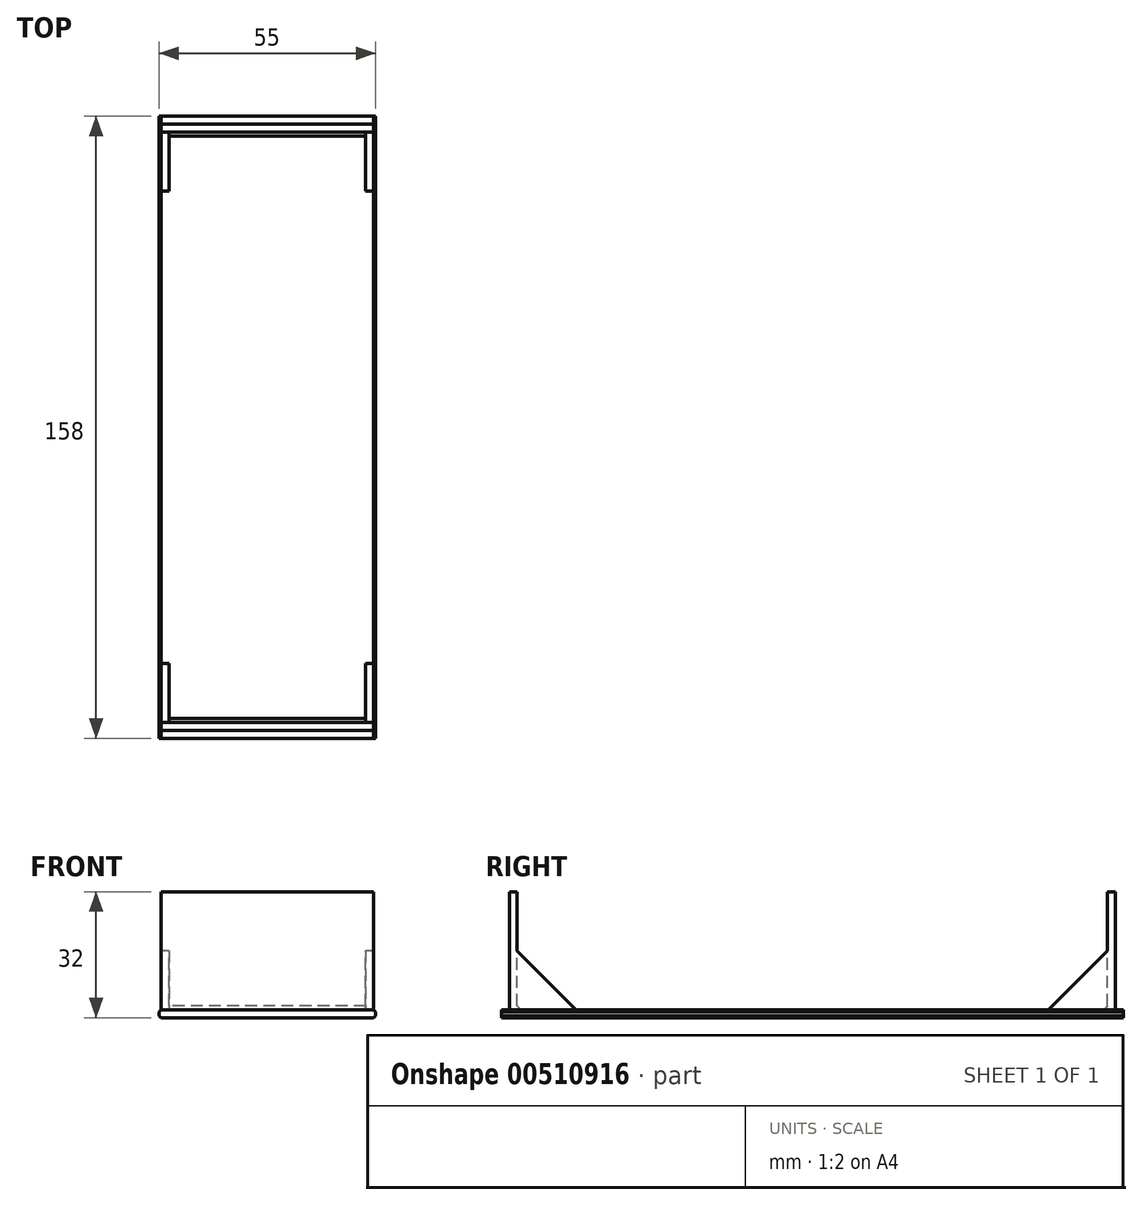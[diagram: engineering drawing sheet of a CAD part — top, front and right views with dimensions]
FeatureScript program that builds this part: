
annotation { "Feature Type Name" : "Feature", "Feature Type Description" : "" }
export const myFeature = defineFeature(function(context is Context, id is Id, definition is map)
    precondition{}
    {
        {
            assignVariable(context, id + "F0", {"name" : "WallThickness", "anyValue" : 2});
        }
        {
            assignVariable(context, id + "F1", {"name" : "InternalWidth", "anyValue" : 50});
        }
        {
            assignVariable(context, id + "F2", {"name" : "SlotWidth", "anyValue" : 0.5});
        }
        {
            var Q0;
            Q0=qCreatedBy(makeId("Right.planeOp"),FACE);
            var sketch = newSketch(context, id + "F3", { "sketchPlane" : qUnion([Q0])});
            skLineSegment(sketch, "E0", {"start": v(-77, 32) * mm, "end": v(-77, 2) * mm});
            skLineSegment(sketch, "E1", {"start": v(-77, 0) * mm, "end": v(0, 0) * mm});
            skLineSegment(sketch, "E2", {"start": v(-75, 2) * mm, "end": v(-75, 32) * mm});
            skLineSegment(sketch, "E3", {"start": v(-75, 32) * mm, "end": v(-77, 32) * mm});
            skLineSegment(sketch, "E4", {"start": v(-75, 2) * mm, "end": v(-77, 2) * mm});
            skLineSegment(sketch, "E5", {"start": v(-75, 2) * mm, "end": v(0, 2) * mm});
            skLineSegment(sketch, "E6", {"start": v(-75, 17) * mm, "end": v(-60, 2) * mm});
            skLineSegment(sketch, "E7.MirrorCS", {"start": v(75, 32) * mm, "end": v(77, 32) * mm});
            skLineSegment(sketch, "E8.MirrorCS", {"start": v(75, 2) * mm, "end": v(77, 2) * mm});
            skLineSegment(sketch, "E9.MirrorCS", {"start": v(75, 2) * mm, "end": v(75, 32) * mm});
            skLineSegment(sketch, "E10.MirrorCS", {"start": v(77, 32) * mm, "end": v(77, 2) * mm});
            skLineSegment(sketch, "E11.MirrorCS", {"start": v(77, 0) * mm, "end": v(0, 0) * mm});
            skLineSegment(sketch, "E12.MirrorCS", {"start": v(75, 17) * mm, "end": v(60, 2) * mm});
            skLineSegment(sketch, "E13.MirrorCS", {"start": v(75, 2) * mm, "end": v(0, 2) * mm});
            skLineSegment(sketch, "E14", {"start": v(-77, 0) * mm, "end": v(-79, 0) * mm});
            skLineSegment(sketch, "E15", {"start": v(-79, 0) * mm, "end": v(-79, 2) * mm});
            skLineSegment(sketch, "E16", {"start": v(-79, 2) * mm, "end": v(-77, 2) * mm});
            skLineSegment(sketch, "E17.MirrorCS", {"start": v(77, 0) * mm, "end": v(79, 0) * mm});
            skLineSegment(sketch, "E18.MirrorCS", {"start": v(79, 2) * mm, "end": v(77, 2) * mm});
            skLineSegment(sketch, "E19.MirrorCS", {"start": v(79, 0) * mm, "end": v(79, 2) * mm});
            skSolve(sketch);
        }
        {
            var Q0;
            {var subQ6=sQuery(id+"F3.wireOp",EDGE,"E1");Q0=makeQuery(id+"F3.imprint","IMPRINT",FACE,{"disambiguationData":[TD([[makeQuery(id+"F3.imprint","IMPRINT",EDGE,{"derivedFrom":subQ6}),1.0]])]});}
            extrude(context, id + "F4", {"entities" : qUnion([Q0]), "endBound" : BoundingType.SYMMETRIC, "depth" : (getVariable(context, 'InternalWidth') + 2 * getVariable(context, 'WallThickness') + 2 * getVariable(context, 'SlotWidth')) * mm});
        }
        {
            var Q0;
            {var subQ0=sQuery(id+"F3.wireOp",EDGE,"E3");Q0=makeQuery(id+"F3.imprint","IMPRINT",FACE,{"disambiguationData":[TD([[makeQuery(id+"F3.imprint","IMPRINT",EDGE,{"derivedFrom":subQ0}),1.0]])]});}
            var Q1;
            {var subQ1=sQuery(id+"F3.wireOp",EDGE,"E7.MirrorCS");Q1=makeQuery(id+"F3.imprint","IMPRINT",FACE,{"disambiguationData":[TD([[makeQuery(id+"F3.imprint","IMPRINT",EDGE,{"derivedFrom":subQ1}),-1.0]])]});}
            var Q2;
            {var subQ3=sQuery(id+"F3.wireOp",EDGE,"E6");Q2=makeQuery(id+"F3.imprint","IMPRINT",FACE,{"disambiguationData":[TD([[makeQuery(id+"F3.imprint","IMPRINT",EDGE,{"derivedFrom":subQ3}),-1.0]])]});}
            var Q3;
            {var subQ3=sQuery(id+"F3.wireOp",EDGE,"E12.MirrorCS");Q3=makeQuery(id+"F3.imprint","IMPRINT",FACE,{"disambiguationData":[TD([[makeQuery(id+"F3.imprint","IMPRINT",EDGE,{"derivedFrom":subQ3}),1.0]])]});}
            extrude(context, id + "F5", {"entities" : qUnion([Q0, Q1, Q2, Q3]), "operationType" : NewBodyOperationType.ADD, "endBound" : BoundingType.SYMMETRIC, "depth" : (getVariable(context, 'InternalWidth') + 2 * getVariable(context, 'WallThickness')) * mm});
        }
        {
            var Q0;
            {var subQ3=sQuery(id+"F3.wireOp",EDGE,"E6");Q0=makeQuery(id+"F3.imprint","IMPRINT",FACE,{"disambiguationData":[TD([[makeQuery(id+"F3.imprint","IMPRINT",EDGE,{"derivedFrom":subQ3}),-1.0]])]});}
            var Q1;
            {var subQ3=sQuery(id+"F3.wireOp",EDGE,"E12.MirrorCS");Q1=makeQuery(id+"F3.imprint","IMPRINT",FACE,{"disambiguationData":[TD([[makeQuery(id+"F3.imprint","IMPRINT",EDGE,{"derivedFrom":subQ3}),1.0]])]});}
            extrude(context, id + "F6", {"entities" : qUnion([Q0, Q1]), "operationType" : NewBodyOperationType.REMOVE, "endBound" : BoundingType.SYMMETRIC, "oppositeDirection" : true, "depth" : (getVariable(context, 'InternalWidth')) * mm});
        }
        {
            var Q0;
            Q0=makeQuery(id+"F6.boolean.opBoolean","COPY",EDGE,{"derivedFrom":makeQuery(id+"F6.opExtrude","SWEPT_EDGE",EDGE,{"disambiguationData":[OSD([sQuery(id+"F3.wireOp",EDGE,"E2"),sQuery(id+"F3.wireOp",EDGE,"E4"),sQuery(id+"F3.wireOp",EDGE,"E5")])]})});
            var Q1;
            Q1=makeQuery(id+"F6.boolean.opBoolean","COPY",EDGE,{"derivedFrom":makeQuery(id+"F6.opExtrude","SWEPT_EDGE",EDGE,{"disambiguationData":[OSD([sQuery(id+"F3.wireOp",EDGE,"E8.MirrorCS"),sQuery(id+"F3.wireOp",EDGE,"E9.MirrorCS"),sQuery(id+"F3.wireOp",EDGE,"E13.MirrorCS")])]})});
            chamfer(context, id + "F7", {"entities" : qUnion([Q0, Q1]), "width" : 1 * mm, "tangentPropagation" : true});
        }
        {
            var Q0;
            Q0=makeQuery(id+"F4.opExtrude","CAP_EDGE",EDGE,{"disambiguationData":[OSD([sQuery(id+"F3.wireOp",EDGE,"E4"),sQuery(id+"F3.wireOp",EDGE,"E5"),sQuery(id+"F3.wireOp",EDGE,"E8.MirrorCS"),sQuery(id+"F3.wireOp",EDGE,"E13.MirrorCS"),sQuery(id+"F3.wireOp",EDGE,"E16"),sQuery(id+"F3.wireOp",EDGE,"E18.MirrorCS")])],"isStart":false});
            var Q1;
            Q1=makeQuery(id+"F4.opExtrude","CAP_EDGE",EDGE,{"disambiguationData":[OSD([sQuery(id+"F3.wireOp",EDGE,"E1"),sQuery(id+"F3.wireOp",EDGE,"E11.MirrorCS"),sQuery(id+"F3.wireOp",EDGE,"E14"),sQuery(id+"F3.wireOp",EDGE,"E17.MirrorCS")])],"isStart":false});
            var Q2;
            Q2=makeQuery(id+"F4.opExtrude","CAP_EDGE",EDGE,{"disambiguationData":[OSD([sQuery(id+"F3.wireOp",EDGE,"E4"),sQuery(id+"F3.wireOp",EDGE,"E5"),sQuery(id+"F3.wireOp",EDGE,"E8.MirrorCS"),sQuery(id+"F3.wireOp",EDGE,"E13.MirrorCS"),sQuery(id+"F3.wireOp",EDGE,"E16"),sQuery(id+"F3.wireOp",EDGE,"E18.MirrorCS")])],"isStart":true});
            var Q3;
            Q3=makeQuery(id+"F4.opExtrude","CAP_EDGE",EDGE,{"disambiguationData":[OSD([sQuery(id+"F3.wireOp",EDGE,"E1"),sQuery(id+"F3.wireOp",EDGE,"E11.MirrorCS"),sQuery(id+"F3.wireOp",EDGE,"E14"),sQuery(id+"F3.wireOp",EDGE,"E17.MirrorCS")])],"isStart":true});
            chamfer(context, id + "F8", {"entities" : qUnion([Q0, Q1, Q2, Q3]), "width" : (getVariable(context, 'WallThickness') / 4) * mm, "tangentPropagation" : true});
        }
    });
